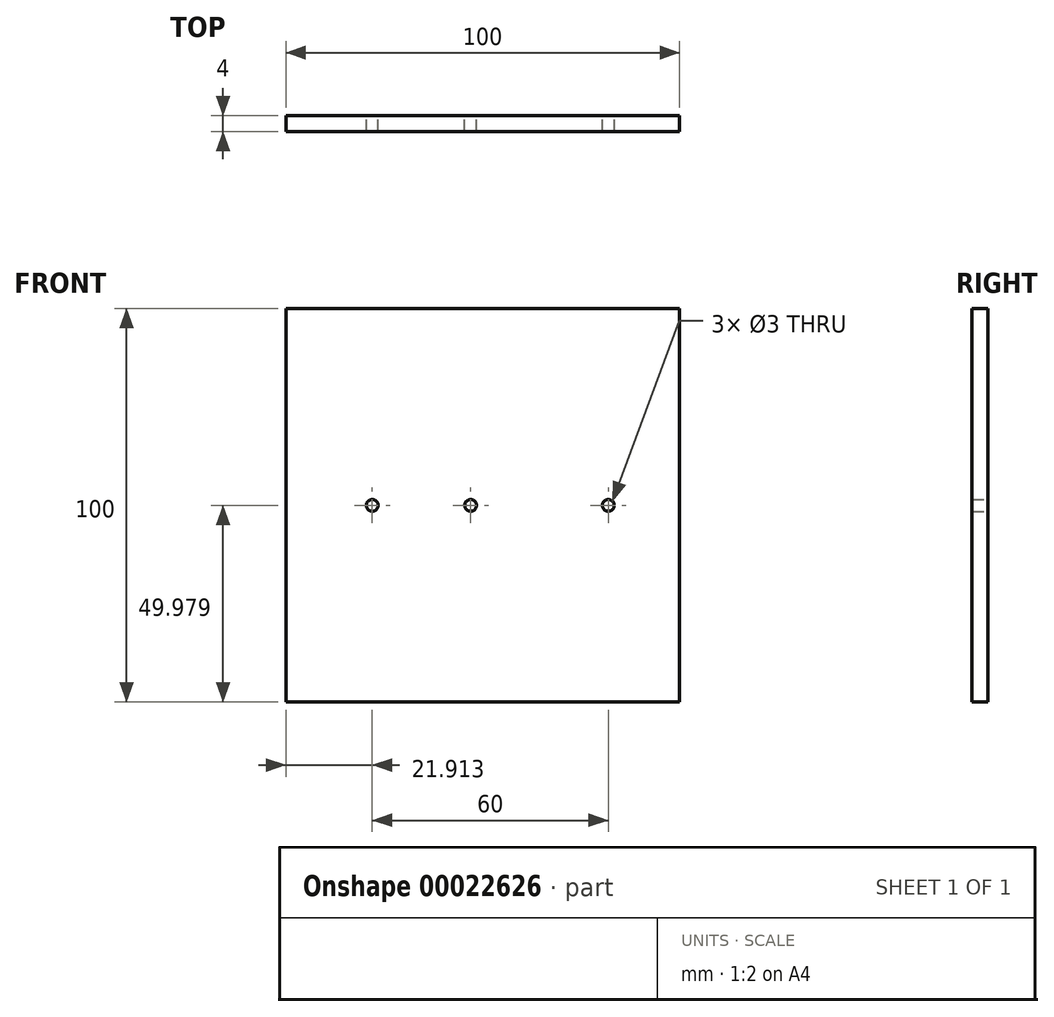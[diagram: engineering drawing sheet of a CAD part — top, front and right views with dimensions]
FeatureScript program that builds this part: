
annotation { "Feature Type Name" : "Feature", "Feature Type Description" : "" }
export const myFeature = defineFeature(function(context is Context, id is Id, definition is map)
    precondition{}
    {
        {
            var Q0;
            Q0=qCreatedBy(makeId("Front.planeOp"),FACE);
            var sketch = newSketch(context, id + "F0", { "sketchPlane" : qUnion([Q0])});
            skLineSegment(sketch, "E0.bottom", {"start": v(-59.03, -21.38) * mm, "end": v(40.97, -21.38) * mm});
            skLineSegment(sketch, "E0.top", {"start": v(-59.03, 78.62) * mm, "end": v(40.97, 78.62) * mm});
            skLineSegment(sketch, "E0.left", {"start": v(-59.03, -21.38) * mm, "end": v(-59.03, 78.62) * mm});
            skLineSegment(sketch, "E0.right", {"start": v(40.97, -21.38) * mm, "end": v(40.97, 78.62) * mm});
            skCircle(sketch, "E1", {"center": v(-37.12, 28.6) * mm, "radius": 1.5 * mm});
            skCircle(sketch, "E2", {"center": v(-12.12, 28.6) * mm, "radius": 1.5 * mm});
            skCircle(sketch, "E3", {"center": v(22.88, 28.6) * mm, "radius": 1.5 * mm});
            skPoint(sketch, "E4.orphan", {"position": v(-59.03, 28.62) * mm});
            skPoint(sketch, "E5.end.orphan", {"position": v(40.97, 28.62) * mm});
            skSolve(sketch);
        }
        {
            var Q0;
            Q0=makeQuery(id+"F0.imprint","IMPRINT",FACE,{"disambiguationData":[TD([[makeQuery(id+"F0.imprint","IMPRINT",EDGE,{"derivedFrom":sQuery(id+"F0.wireOp",EDGE,"E0.bottom")}),1.0]])]});
            extrude(context, id + "F1", {"entities" : qUnion([Q0]), "depth" : 4 * mm});
        }
    });
